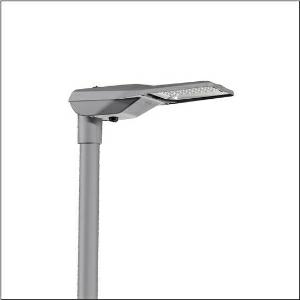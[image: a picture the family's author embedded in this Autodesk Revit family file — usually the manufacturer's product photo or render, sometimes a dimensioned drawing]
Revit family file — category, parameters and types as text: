
# Revit family: streetlight_sl_21_iq_mini___p0_8ab_5xe2r31y08hb_a9b9
name_source: partatom
category: Lighting Fixtures
units: mm (PartAtom-declared; Revit-internal decimal feet)

## family parameters
Cut with Voids When Loaded = No
Host = Face
Light Source = No
Part Type = Normal
Room Calculation Point = No
Round Connector Dimension = Use Diameter
Shared = No

## types (1)
- --- (1 x LED, 8460 lm, 71 W, 3000K)
    Apparent Load = 71 VA
    CIE Flux Codes = 36 71 98 100 100
    Color Rendering = 70
    Color Temperature = 3000K
    Default Elevation = 1800 mm
    Description = Streetlight SL 21 iQ mini, mast luminaire, primary light control with lens, of PMMA, primary optical cover: cover, of toughened safety glass, transparent, light distribution: P0.8aB, light emission: direct distribution, primary light characteristic: asymmetric, installation type: post-top, side-entry, LED, High Power LED, rated luminous flux: 8.460lm, luminous efficacy: 119lm/W, light colour: 730, colour temperature: 3000K, control gear: iQ-Street Remote, D4i with power reduction, control: pre-setting: logarithmic dimming characteristic, Street-Remote, Auto-Match, Temp-Guard, Lumen-Switch, Night-Set, Smart-Wire, Light-Fading, Desk-Remote (wireless, voltage-free reading and setting of iQ features in the workshop via application-optimized NFC function/RFID function), optimised constant luminous flux control (CLO 2.0), mains connection: 220..240V, AC, 50/60Hz, start of lifetime: 71W, end of service life: 75W, reduction: 30W, luminaire housing, of diecast aluminium, powder-coated, Siteco® metallic grey (DB 702S), corrosivity category C5 mid according to DIN EN ISO 12944, please order mast flange separately, inclination adjustable: 0°, 5°, 10°, 15°, sealing non-destructively replaceable, multi-level sealing system, length: 628mm, width: 235mm, height: 110mm, mast flange for spigot size: 42mm (side-entry): 5XC10008XM4, 60/48mm (side-entry/post-top): 5XC10108XM2, 76/60mm (side-entry/post-top): 5XC10108XM1, mounting height: 4..8m, Smart Interface below and above, protection rating (complete): IP66, insulation class (complete): insulation class II (safety insulation), certification: CE, ENEC, ENEC+, VDE, impact resistance: IK10, permissible operating ambient temperature for outdoor applications: -40..+50°C, standard-compliant lighting for roads and squares, packaging unit: 1 piece

Light Distribution: P0.8aB
    Height = 110 mm
    Lamp = 1 x LED
    Lamp Light Flux = 8460 lm
    Lamp Power = 71 W
    Lamp count = 1
    Length = 625 mm
    Luminous efficacy = 119 lm/W
    Manufacturer = Siteco
    ModVariant = No
    Model = 5XE2R31Y08HB
    Number of Poles = 1
    OnlyDefault = Yes
    Power Factor = 1
    Product Name = Streetlight SL 21 iQ mini | P0.8aB
    Product group = mast luminaire | pylon top
    ProductGroupID = 6100
    Protection Class = Protection class II
    Protection Degree = IP 66
    RLX_Detail_Level = 1
    RLX_Emergency_Light_Flux = 0 lm
    RLX_Emergency_Type = 0
    RLX_Emergency_Type_DB = No
    RlxData = <blob elided: 26289 chars, md5=09fb2b96>
    Socket = socket
    Standby Power = 0 W
    System Light Flux = 8460 lm
    System Power = 71 W
    Type Comments = factory setting: luminous flux: 100 % | dim-lin: 254 | 716 mA
    Type Image = l_1003514.jpg
    URL = http://relux.com
    VarID = @adj_075310
    Voltage = 0 V
    Weight = 0.00 kg
    Width = 234 mm

## geometry (parser evidence)
native form markers: Blend x4, Sweep x10
no freeform markers — native parametric forms only
